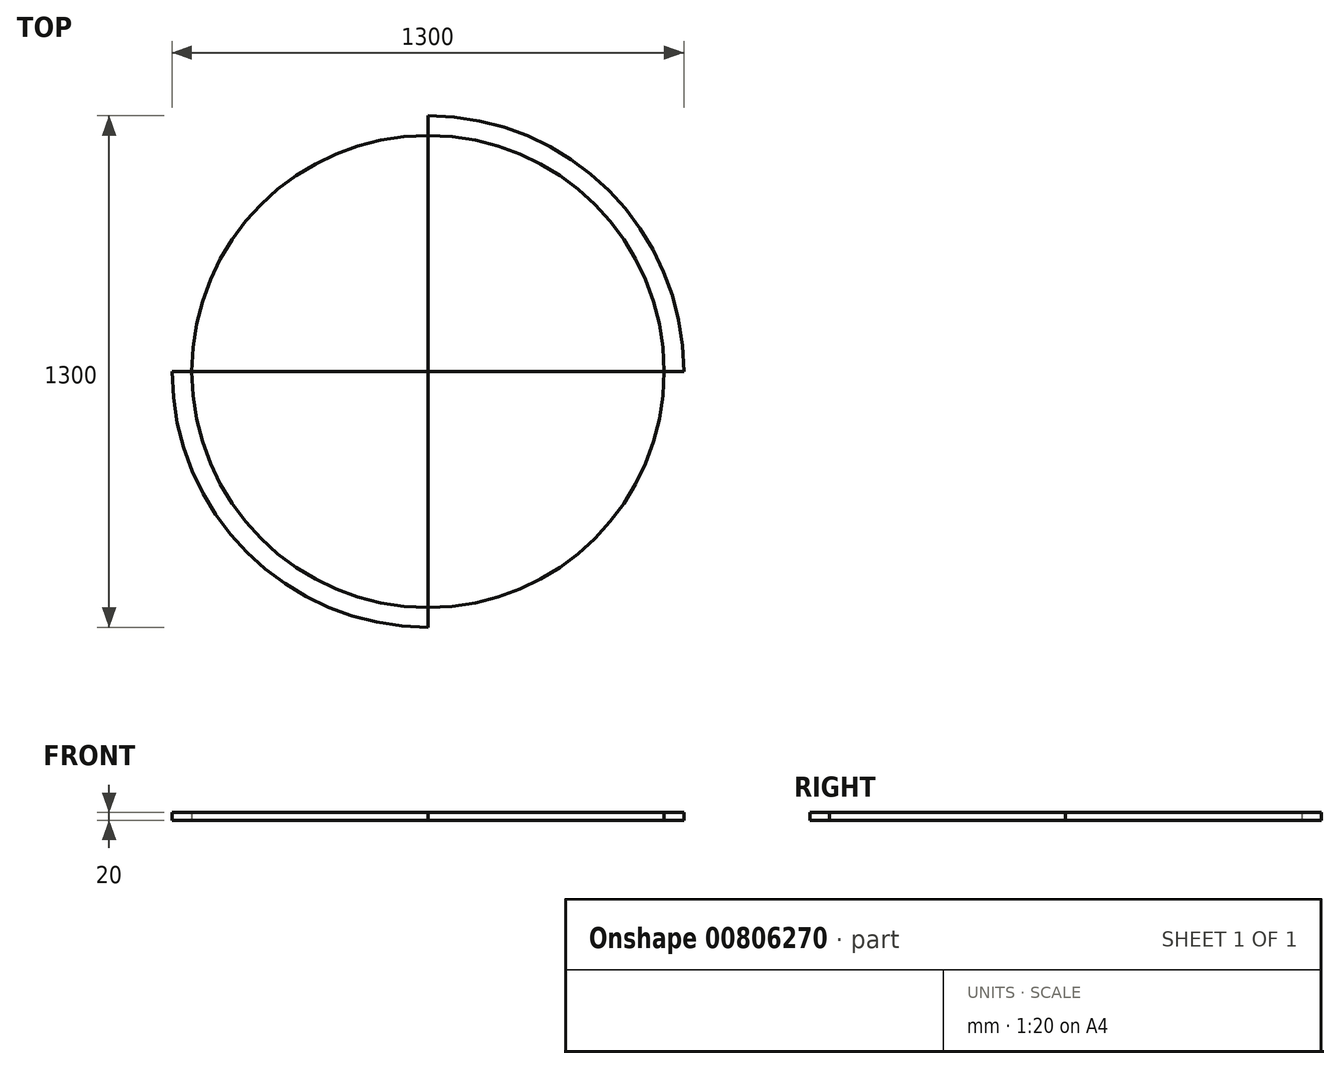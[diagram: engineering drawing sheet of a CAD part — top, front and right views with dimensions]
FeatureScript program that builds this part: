
annotation { "Feature Type Name" : "Feature", "Feature Type Description" : "" }
export const myFeature = defineFeature(function(context is Context, id is Id, definition is map)
    precondition{}
    {
        {
            var Q0;
            Q0=qCreatedBy(makeId("Top.planeOp"),FACE);
            var sketch = newSketch(context, id + "F0", { "sketchPlane" : qUnion([Q0])});
            skArc(sketch, "E0", {"start": v(-600, 0) * mm, "mid": v(-424.26, -424.26) * mm, "end": v(0, -600) * mm});
            skArc(sketch, "E1", {"start": v(-700, 0) * mm, "mid": v(-494.97, -494.97) * mm, "end": v(0, -700) * mm});
            skLineSegment(sketch, "E2", {"start": v(0, 0) * mm, "end": v(0, -700) * mm});
            skLineSegment(sketch, "E3", {"start": v(-600, 0) * mm, "end": v(-700, 0) * mm});
            skLineSegment(sketch, "E4", {"start": v(-600, 0) * mm, "end": v(0, 0) * mm});
            skLineSegment(sketch, "E5.MirrorCS", {"start": v(600, 0) * mm, "end": v(700, 0) * mm});
            skArc(sketch, "E6.MirrorCS", {"start": v(600, 0) * mm, "mid": v(424.26, -424.26) * mm, "end": v(0, -600) * mm});
            skArc(sketch, "E7.MirrorCS", {"start": v(700, 0) * mm, "mid": v(494.97, -494.97) * mm, "end": v(0, -700) * mm});
            skLineSegment(sketch, "E8.MirrorCS", {"start": v(600, 0) * mm, "end": v(0, 0) * mm});
            skLineSegment(sketch, "E9.MirrorCS", {"start": v(0, 0) * mm, "end": v(0, 700) * mm});
            skArc(sketch, "E10.MirrorCS", {"start": v(-600, 0) * mm, "mid": v(-424.26, 424.26) * mm, "end": v(0, 600) * mm});
            skArc(sketch, "E11.MirrorCS", {"start": v(600, 0) * mm, "mid": v(424.26, 424.26) * mm, "end": v(0, 600) * mm});
            skArc(sketch, "E12.MirrorCS", {"start": v(700, 0) * mm, "mid": v(494.97, 494.97) * mm, "end": v(0, 700) * mm});
            skArc(sketch, "E13.MirrorCS", {"start": v(-700, 0) * mm, "mid": v(-494.97, 494.97) * mm, "end": v(0, 700) * mm});
            skCircle(sketch, "E14", {"center": v(0, 0) * mm, "radius": 650 * mm});
            skSolve(sketch);
        }
        {
            var Q0;
            {var subQ0=sQuery(id+"F0.wireOp",EDGE,"E0");Q0=makeQuery(id+"F0.imprint","IMPRINT",FACE,{"disambiguationData":[TD([[makeQuery(id+"F0.imprint","IMPRINT",EDGE,{"derivedFrom":subQ0}),-1.0]])]});}
            var Q1;
            {var subQ0=sQuery(id+"F0.wireOp",EDGE,"E10.MirrorCS");Q1=makeQuery(id+"F0.imprint","IMPRINT",FACE,{"disambiguationData":[TD([[makeQuery(id+"F0.imprint","IMPRINT",EDGE,{"derivedFrom":subQ0}),1.0]])]});}
            var Q2;
            {var subQ0=sQuery(id+"F0.wireOp",EDGE,"E11.MirrorCS");Q2=makeQuery(id+"F0.imprint","IMPRINT",FACE,{"disambiguationData":[TD([[makeQuery(id+"F0.imprint","IMPRINT",EDGE,{"derivedFrom":subQ0}),-1.0]])]});}
            var Q3;
            {var subQ0=sQuery(id+"F0.wireOp",EDGE,"E6.MirrorCS");Q3=makeQuery(id+"F0.imprint","IMPRINT",FACE,{"disambiguationData":[TD([[makeQuery(id+"F0.imprint","IMPRINT",EDGE,{"derivedFrom":subQ0}),1.0]])]});}
            extrude(context, id + "F1", {"entities" : qUnion([Q0, Q1, Q2, Q3]), "depth" : 20 * mm, "offsetDistance" : 25 * mm});
        }
    });
